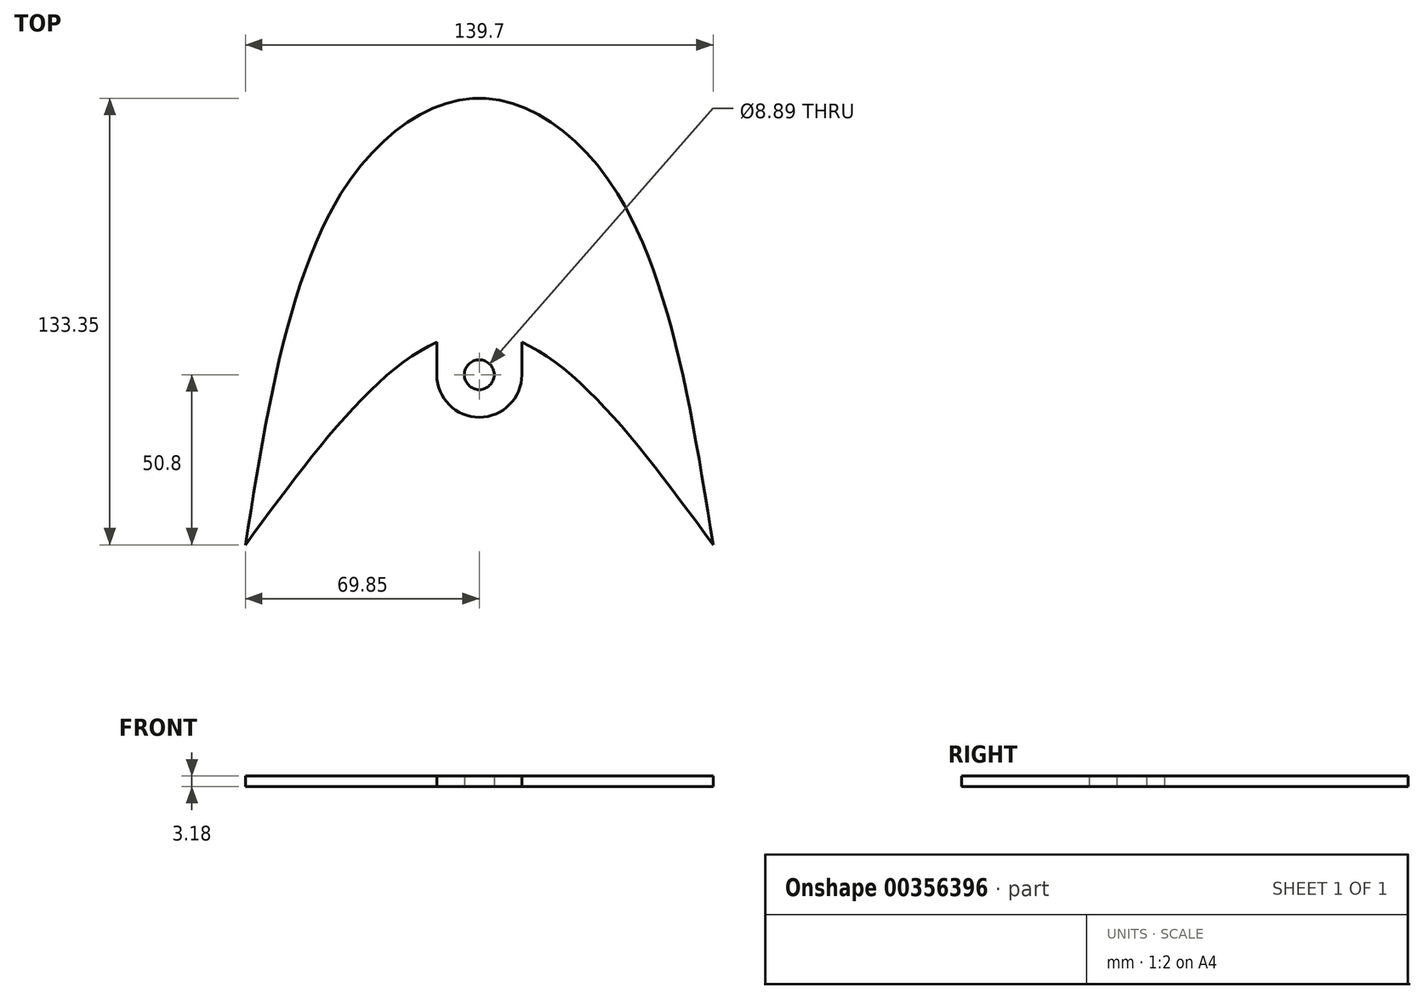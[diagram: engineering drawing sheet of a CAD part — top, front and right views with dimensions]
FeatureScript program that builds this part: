
annotation { "Feature Type Name" : "Feature", "Feature Type Description" : "" }
export const myFeature = defineFeature(function(context is Context, id is Id, definition is map)
    precondition{}
    {
        {
            var Q0;
            Q0=qCreatedBy(makeId("Top.planeOp"),FACE);
            var sketch = newSketch(context, id + "F0", { "sketchPlane" : qUnion([Q0])});
            skLineSegment(sketch, "E0", {"start": v(-69.85, -63.5) * mm, "end": v(-69.85, 0) * mm});
            skLineSegment(sketch, "E1", {"start": v(69.85, 0) * mm, "end": v(69.85, -63.5) * mm});
            skPoint(sketch, "E2", {"position": v(0, 69.85) * mm});
            skLineSegment(sketch, "E3", {"start": v(0, 0) * mm, "end": v(-41.3, 41.3) * mm});
            skLineSegment(sketch, "E4", {"start": v(0, 0) * mm, "end": v(41.3, 41.3) * mm});
            skFitSpline(sketch, "E5", {"points": [v(-69.85, -63.5) * mm, v(-41.3, 41.3) * mm, v(0, 69.85) * mm, v(41.3, 41.3) * mm, v(69.85, -63.5) * mm], "startDerivative": vector(63.67, 398.68) * mm, "endDerivative": vector(63.67, -398.68) * mm});
            skPoint(sketch, "E6", {"position": v(-57.7, 0) * mm});
            skFitSpline(sketch, "E7", {"points": [v(-69.85, -63.5) * mm, v(0, 0) * mm, v(69.85, -63.5) * mm], "startDerivative": vector(139.7, 190.5) * mm, "endDerivative": vector(139.7, -190.5) * mm});
            skLineSegment(sketch, "E8", {"start": v(-12.7, 0) * mm, "end": v(-12.7, -12.7) * mm});
            skLineSegment(sketch, "E9", {"start": v(12.7, 0) * mm, "end": v(12.7, -12.7) * mm});
            skArc(sketch, "E10", {"start": v(-12.7, -12.7) * mm, "mid": v(0, -25.4) * mm, "end": v(12.7, -12.7) * mm});
            skLineSegment(sketch, "E11", {"start": v(-12.7, 0) * mm, "end": v(12.7, 0) * mm});
            skCircle(sketch, "E12", {"center": v(0, -12.7) * mm, "radius": 4.45 * mm});
            skSolve(sketch);
        }
        {
            var Q0;
            {var subQ3=sQuery(id+"F0.wireOp",EDGE,"E3");Q0=makeQuery(id+"F0.imprint","IMPRINT",FACE,{"disambiguationData":[TD([[makeQuery(id+"F0.imprint","IMPRINT",EDGE,{"derivedFrom":subQ3}),1.0]])]});}
            var Q1;
            {var subQ0=sQuery(id+"F0.wireOp",EDGE,"E3");Q1=makeQuery(id+"F0.imprint","IMPRINT",FACE,{"disambiguationData":[TD([[makeQuery(id+"F0.imprint","IMPRINT",EDGE,{"derivedFrom":subQ0}),-1.0]])]});}
            var Q2;
            {var subQ5=sQuery(id+"F0.wireOp",EDGE,"E4");Q2=makeQuery(id+"F0.imprint","IMPRINT",FACE,{"disambiguationData":[TD([[makeQuery(id+"F0.imprint","IMPRINT",EDGE,{"derivedFrom":subQ5}),-1.0]])]});}
            var Q3;
            {var subQ1=sQuery(id+"F0.wireOp",EDGE,"E7");var subQ3=sQuery(id+"F0.wireOp",EDGE,"E9");var subQ4=makeQuery(id+"F0.imprint","INTERSECT",VERTEX,{"derivedFrom":[subQ1,subQ3]});Q3=makeQuery(id+"F0.imprint","IMPRINT",FACE,{"disambiguationData":[TD([[makeQuery(id+"F0.imprint","IMPRINT",EDGE,{"disambiguationData":[TD([[subQ4,1.0]])],"derivedFrom":subQ3}),-1.0]])]});}
            var Q4;
            {var subQ1=sQuery(id+"F0.wireOp",EDGE,"E7");var subQ3=sQuery(id+"F0.wireOp",EDGE,"E8");var subQ4=makeQuery(id+"F0.imprint","INTERSECT",VERTEX,{"derivedFrom":[subQ1,subQ3]});Q4=makeQuery(id+"F0.imprint","IMPRINT",FACE,{"disambiguationData":[TD([[makeQuery(id+"F0.imprint","IMPRINT",EDGE,{"disambiguationData":[TD([[subQ4,1.0]])],"derivedFrom":subQ3}),1.0]])]});}
            var Q5;
            {var subQ3=sQuery(id+"F0.wireOp",EDGE,"E10");Q5=makeQuery(id+"F0.imprint","IMPRINT",FACE,{"disambiguationData":[TD([[makeQuery(id+"F0.imprint","IMPRINT",EDGE,{"derivedFrom":subQ3}),1.0]])]});}
            extrude(context, id + "F1", {"entities" : qUnion([Q0, Q1, Q2, Q3, Q4, Q5]), "depth" : 3.17 * mm, "offsetDistance" : 25.4 * mm});
        }
    });
